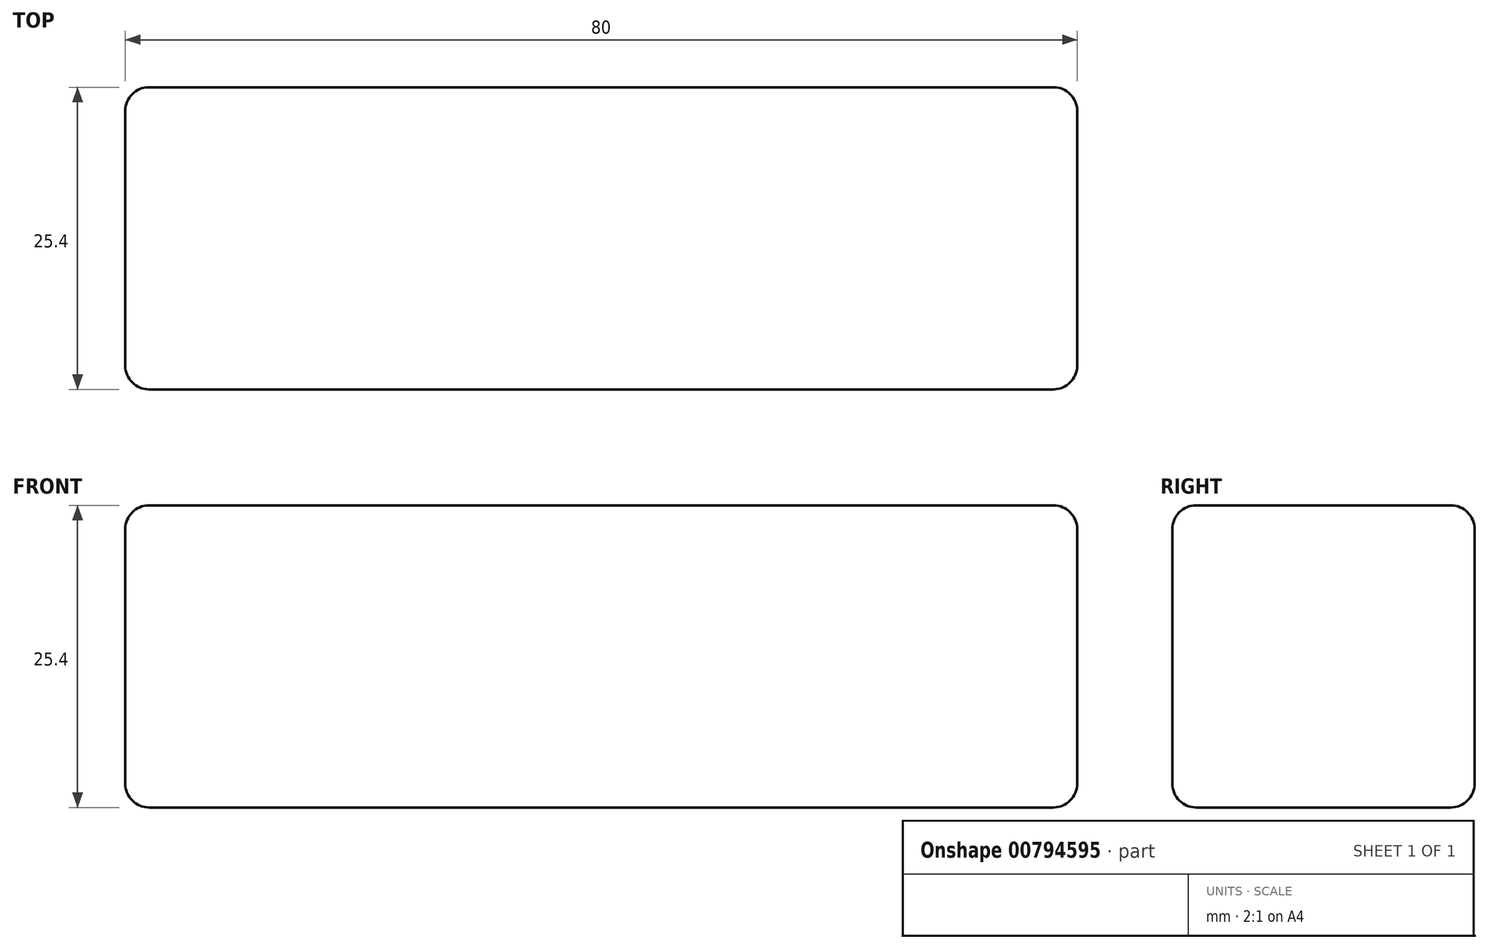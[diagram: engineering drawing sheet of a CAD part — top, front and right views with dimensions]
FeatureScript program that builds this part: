
annotation { "Feature Type Name" : "Feature", "Feature Type Description" : "" }
export const myFeature = defineFeature(function(context is Context, id is Id, definition is map)
    precondition{}
    {
        {
            var Q0;
            Q0=qCreatedBy(makeId("Front.planeOp"),FACE);
            var sketch = newSketch(context, id + "F0", { "sketchPlane" : qUnion([Q0])});
            skLineSegment(sketch, "E0.bottom", {"start": v(0, 0) * mm, "end": v(-80, 0) * mm});
            skLineSegment(sketch, "E0.top", {"start": v(0, 25.4) * mm, "end": v(-80, 25.4) * mm});
            skLineSegment(sketch, "E0.left", {"start": v(0, 0) * mm, "end": v(0, 25.4) * mm});
            skLineSegment(sketch, "E0.right", {"start": v(-80, 0) * mm, "end": v(-80, 25.4) * mm});
            skSolve(sketch);
        }
        {
            var Q0;
            Q0 = qSketchRegion(id + "F0", true);
            extrude(context, id + "F1", {"entities" : qUnion([Q0]), "depth" : 25.4 * mm, "offsetDistance" : 25 * mm});
        }
        {
            var Q0;
            Q0=makeQuery(id+"F1.opExtrude","CAP_EDGE",EDGE,{"disambiguationData":[OSD([sQuery(id+"F0.wireOp",EDGE,"E0.top")])],"isStart":false});
            var Q1;
            Q1=makeQuery(id+"F1.opExtrude","CAP_EDGE",EDGE,{"disambiguationData":[OSD([sQuery(id+"F0.wireOp",EDGE,"E0.right")])],"isStart":false});
            var Q2;
            Q2=makeQuery(id+"F1.opExtrude","SWEPT_EDGE",EDGE,{"disambiguationData":[OSD([sQuery(id+"F0.wireOp",EDGE,"E0.top"),sQuery(id+"F0.wireOp",EDGE,"E0.right")])]});
            var Q3;
            Q3=makeQuery(id+"F1.opExtrude","SWEPT_EDGE",EDGE,{"disambiguationData":[OSD([sQuery(id+"F0.wireOp",EDGE,"E0.bottom"),sQuery(id+"F0.wireOp",EDGE,"E0.right")])]});
            var Q4;
            Q4=makeQuery(id+"F1.opExtrude","CAP_EDGE",EDGE,{"disambiguationData":[OSD([sQuery(id+"F0.wireOp",EDGE,"E0.bottom")])],"isStart":false});
            var Q5;
            Q5=makeQuery(id+"F1.opExtrude","CAP_EDGE",EDGE,{"disambiguationData":[OSD([sQuery(id+"F0.wireOp",EDGE,"E0.left")])],"isStart":false});
            var Q6;
            Q6=makeQuery(id+"F1.opExtrude","SWEPT_EDGE",EDGE,{"disambiguationData":[OSD([sQuery(id+"F0.wireOp",EDGE,"E0.top"),sQuery(id+"F0.wireOp",EDGE,"E0.left")])]});
            var Q7;
            Q7=makeQuery(id+"F1.opExtrude","CAP_EDGE",EDGE,{"disambiguationData":[OSD([sQuery(id+"F0.wireOp",EDGE,"E0.right")])],"isStart":true});
            var Q8;
            Q8=makeQuery(id+"F1.opExtrude","CAP_EDGE",EDGE,{"disambiguationData":[OSD([sQuery(id+"F0.wireOp",EDGE,"E0.bottom")])],"isStart":true});
            var Q9;
            Q9=makeQuery(id+"F1.opExtrude","CAP_EDGE",EDGE,{"disambiguationData":[OSD([sQuery(id+"F0.wireOp",EDGE,"E0.left")])],"isStart":true});
            var Q10;
            Q10=makeQuery(id+"F1.opExtrude","CAP_EDGE",EDGE,{"disambiguationData":[OSD([sQuery(id+"F0.wireOp",EDGE,"E0.top")])],"isStart":true});
            var Q11;
            Q11=makeQuery(id+"F1.opExtrude","SWEPT_EDGE",EDGE,{"disambiguationData":[OSD([sQuery(id+"F0.wireOp",EDGE,"E0.bottom"),sQuery(id+"F0.wireOp",EDGE,"E0.left")])]});
            fillet(context, id + "F2", {"entities" : qUnion([Q0, Q1, Q2, Q3, Q4, Q5, Q6, Q7, Q8, Q9, Q10, Q11]), "radius" : 2 * mm, "tangentPropagation" : true, "allowEdgeOverflow" : false});
        }
    });
